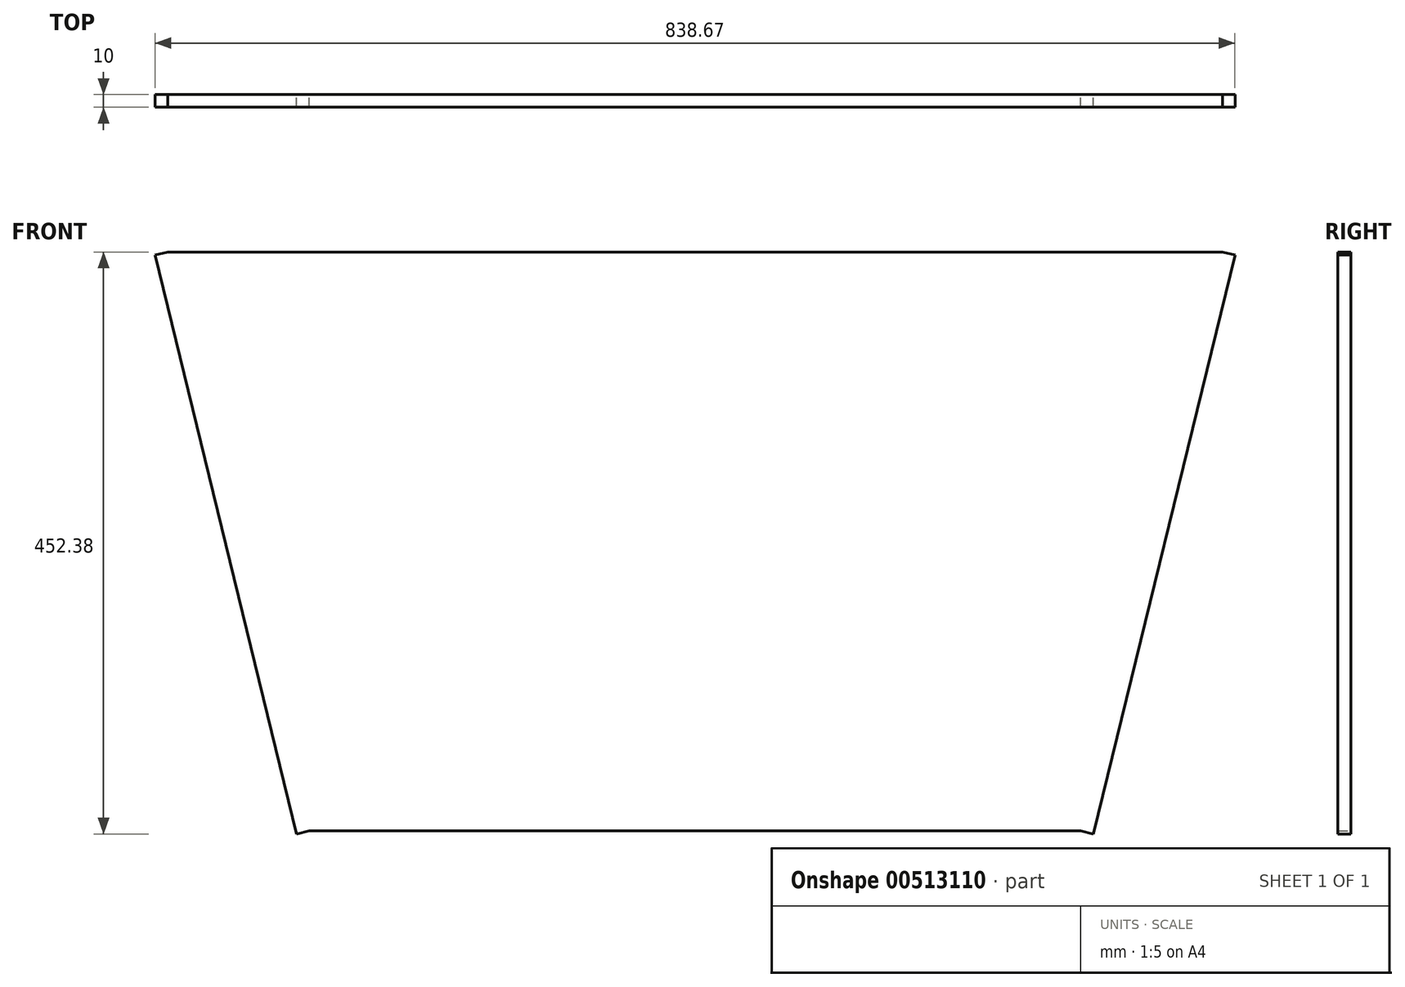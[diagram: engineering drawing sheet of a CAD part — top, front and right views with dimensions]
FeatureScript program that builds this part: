
annotation { "Feature Type Name" : "Feature", "Feature Type Description" : "" }
export const myFeature = defineFeature(function(context is Context, id is Id, definition is map)
    precondition{}
    {
        {
            var Q0;
            Q0=qCreatedBy(makeId("Front.planeOp"),FACE);
            var sketch = newSketch(context, id + "F0", { "sketchPlane" : qUnion([Q0])});
            skLineSegment(sketch, "E0.1", {"start": v(-436.34, 213.95) * mm, "end": v(-436.34, -176.05) * mm});
            skLineSegment(sketch, "E0.3", {"start": v(103.66, 213.95) * mm, "end": v(103.66, -176.05) * mm});
            skLineSegment(sketch, "E1", {"start": v(-465.58, -206.05) * mm, "end": v(133.66, -206.05) * mm});
            skLineSegment(sketch, "E2", {"start": v(-436.34, -176.05) * mm, "end": v(103.66, -176.05) * mm});
            skLineSegment(sketch, "E3", {"start": v(-436.34, 213.95) * mm, "end": v(103.66, 213.95) * mm});
            skLineSegment(sketch, "E4", {"start": v(-465.58, 243.95) * mm, "end": v(133.66, 243.95) * mm});
            skLineSegment(sketch, "E5", {"start": v(-465.58, 243.95) * mm, "end": v(-575.58, 243.95) * mm});
            skLineSegment(sketch, "E6", {"start": v(133.66, 243.95) * mm, "end": v(243.66, 243.95) * mm});
            skLineSegment(sketch, "E7", {"start": v(-575.58, 243.95) * mm, "end": v(-465.58, -206.05) * mm});
            skLineSegment(sketch, "E8", {"start": v(243.66, 243.95) * mm, "end": v(133.66, -206.05) * mm});
            skLineSegment(sketch, "E9.0", {"start": v(-537.36, 213.95) * mm, "end": v(-495.58, 43.02) * mm});
            skLineSegment(sketch, "E9.1", {"start": v(-495.58, 213.95) * mm, "end": v(-537.36, 213.95) * mm});
            skLineSegment(sketch, "E9.2", {"start": v(-495.58, 213.95) * mm, "end": v(-495.58, 43.02) * mm});
            skLineSegment(sketch, "E10.0", {"start": v(205.44, 213.95) * mm, "end": v(163.66, 43.02) * mm});
            skLineSegment(sketch, "E10.1", {"start": v(163.66, 213.95) * mm, "end": v(205.44, 213.95) * mm});
            skLineSegment(sketch, "E10.2", {"start": v(163.66, 213.95) * mm, "end": v(163.66, 43.02) * mm});
            skSolve(sketch);
        }
        {
            var Q0;
            Q0=makeQuery(id+"F0.imprint","IMPRINT",FACE,{"disambiguationData":[TD([[makeQuery(id+"F0.imprint","IMPRINT",EDGE,{"derivedFrom":sQuery(id+"F0.wireOp",EDGE,"E0.1")}),-1.0]])]});
            extrude(context, id + "F1", {"entities" : qUnion([Q0]), "depth" : 10 * mm, "offsetDistance" : 25 * mm});
        }
        {
            var Q0;
            Q0=makeQuery(id+"F1.opExtrude","CAP_FACE",FACE,{"disambiguationData":[OSD([sQuery(id+"F0.wireOp",EDGE,"E0.1"),sQuery(id+"F0.wireOp",EDGE,"E0.3"),sQuery(id+"F0.wireOp",EDGE,"E1"),sQuery(id+"F0.wireOp",EDGE,"E2"),sQuery(id+"F0.wireOp",EDGE,"E3"),sQuery(id+"F0.wireOp",EDGE,"E4"),sQuery(id+"F0.wireOp",EDGE,"E5"),sQuery(id+"F0.wireOp",EDGE,"E6"),sQuery(id+"F0.wireOp",EDGE,"E7"),sQuery(id+"F0.wireOp",EDGE,"E8"),sQuery(id+"F0.wireOp",EDGE,"E9.0"),sQuery(id+"F0.wireOp",EDGE,"E9.1"),sQuery(id+"F0.wireOp",EDGE,"E9.2"),sQuery(id+"F0.wireOp",EDGE,"E10.0"),sQuery(id+"F0.wireOp",EDGE,"E10.1"),sQuery(id+"F0.wireOp",EDGE,"E10.2")])],"isStart":false});
            var sketch = newSketch(context, id + "F2", { "sketchPlane" : qUnion([Q0])});
            skLineSegment(sketch, "E11.bottom", {"start": v(-436.34, 213.95) * mm, "end": v(-356.34, 213.95) * mm});
            skLineSegment(sketch, "E11.top", {"start": v(-436.34, 133.95) * mm, "end": v(-356.34, 133.95) * mm});
            skLineSegment(sketch, "E11.left", {"start": v(-436.34, 213.95) * mm, "end": v(-436.34, 133.95) * mm});
            skLineSegment(sketch, "E11.right", {"start": v(-356.34, 213.95) * mm, "end": v(-356.34, 133.95) * mm});
            skLineSegment(sketch, "E12.bottom", {"start": v(103.66, 213.95) * mm, "end": v(23.66, 213.95) * mm});
            skLineSegment(sketch, "E12.top", {"start": v(103.66, 133.95) * mm, "end": v(23.66, 133.95) * mm});
            skLineSegment(sketch, "E12.left", {"start": v(103.66, 213.95) * mm, "end": v(103.66, 133.95) * mm});
            skLineSegment(sketch, "E12.right", {"start": v(23.66, 213.95) * mm, "end": v(23.66, 133.95) * mm});
            skLineSegment(sketch, "E13.bottom", {"start": v(-436.34, -176.05) * mm, "end": v(-356.34, -176.05) * mm});
            skLineSegment(sketch, "E13.top", {"start": v(-436.34, -96.05) * mm, "end": v(-356.34, -96.05) * mm});
            skLineSegment(sketch, "E13.left", {"start": v(-436.34, -176.05) * mm, "end": v(-436.34, -96.05) * mm});
            skLineSegment(sketch, "E13.right", {"start": v(-356.34, -176.05) * mm, "end": v(-356.34, -96.05) * mm});
            skLineSegment(sketch, "E14.bottom", {"start": v(103.66, -176.05) * mm, "end": v(23.66, -176.05) * mm});
            skLineSegment(sketch, "E14.top", {"start": v(103.66, -96.05) * mm, "end": v(23.66, -96.05) * mm});
            skLineSegment(sketch, "E14.left", {"start": v(103.66, -176.05) * mm, "end": v(103.66, -96.05) * mm});
            skLineSegment(sketch, "E14.right", {"start": v(23.66, -176.05) * mm, "end": v(23.66, -96.05) * mm});
            skCircle(sketch, "E15", {"center": v(-396.34, -136.05) * mm, "radius": 15 * mm});
            skCircle(sketch, "E16", {"center": v(-396.34, 198.82) * mm, "radius": 15 * mm});
            skCircle(sketch, "E17", {"center": v(63.66, 198.82) * mm, "radius": 15 * mm});
            skCircle(sketch, "E18", {"center": v(63.66, -136.05) * mm, "radius": 15 * mm});
            skSolve(sketch);
        }
        {
            var Q0;
            Q0=makeQuery(id+"F2.imprint","IMPRINT",FACE,{"disambiguationData":[TD([[makeQuery(id+"F2.imprint","IMPRINT",EDGE,{"derivedFrom":sQuery(id+"F2.wireOp",EDGE,"E11.bottom")}),-1.0]])]});
            var Q1;
            Q1=makeQuery(id+"F2.imprint","IMPRINT",FACE,{"disambiguationData":[TD([[makeQuery(id+"F2.imprint","IMPRINT",EDGE,{"derivedFrom":sQuery(id+"F2.wireOp",EDGE,"E12.bottom")}),-1.0]])]});
            var Q2;
            Q2=makeQuery(id+"F2.imprint","IMPRINT",FACE,{"disambiguationData":[TD([[makeQuery(id+"F2.imprint","IMPRINT",EDGE,{"derivedFrom":sQuery(id+"F2.wireOp",EDGE,"E14.bottom")}),1.0]])]});
            var Q3;
            Q3=makeQuery(id+"F2.imprint","IMPRINT",FACE,{"disambiguationData":[TD([[makeQuery(id+"F2.imprint","IMPRINT",EDGE,{"derivedFrom":sQuery(id+"F2.wireOp",EDGE,"E13.bottom")}),1.0]])]});
            extrude(context, id + "F3", {"entities" : qUnion([Q0, Q1, Q2, Q3]), "operationType" : NewBodyOperationType.ADD, "oppositeDirection" : true, "depth" : 10 * mm, "offsetDistance" : 25 * mm});
        }
        {
            var Q0;
            Q0=makeQuery(id+"F3.boolean.opBoolean","MERGE",FACE,{"derivedFrom":[makeQuery(id+"F1.opExtrude","CAP_FACE",FACE,{"disambiguationData":[OSD([sQuery(id+"F0.wireOp",EDGE,"E0.1"),sQuery(id+"F0.wireOp",EDGE,"E0.3"),sQuery(id+"F0.wireOp",EDGE,"E1"),sQuery(id+"F0.wireOp",EDGE,"E2"),sQuery(id+"F0.wireOp",EDGE,"E3"),sQuery(id+"F0.wireOp",EDGE,"E4"),sQuery(id+"F0.wireOp",EDGE,"E5"),sQuery(id+"F0.wireOp",EDGE,"E6"),sQuery(id+"F0.wireOp",EDGE,"E7"),sQuery(id+"F0.wireOp",EDGE,"E8"),sQuery(id+"F0.wireOp",EDGE,"E9.0"),sQuery(id+"F0.wireOp",EDGE,"E9.1"),sQuery(id+"F0.wireOp",EDGE,"E9.2"),sQuery(id+"F0.wireOp",EDGE,"E10.0"),sQuery(id+"F0.wireOp",EDGE,"E10.1"),sQuery(id+"F0.wireOp",EDGE,"E10.2")])],"isStart":false}),makeQuery(id+"F3.opExtrude","CAP_FACE",FACE,{"disambiguationData":[OSD([sQuery(id+"F2.wireOp",EDGE,"E11.bottom"),sQuery(id+"F2.wireOp",EDGE,"E11.top"),sQuery(id+"F2.wireOp",EDGE,"E11.left"),sQuery(id+"F2.wireOp",EDGE,"E11.right"),sQuery(id+"F2.wireOp",EDGE,"E16")])],"isStart":true}),makeQuery(id+"F3.opExtrude","CAP_FACE",FACE,{"disambiguationData":[OSD([sQuery(id+"F2.wireOp",EDGE,"E12.bottom"),sQuery(id+"F2.wireOp",EDGE,"E12.top"),sQuery(id+"F2.wireOp",EDGE,"E12.left"),sQuery(id+"F2.wireOp",EDGE,"E12.right"),sQuery(id+"F2.wireOp",EDGE,"E17")])],"isStart":true}),makeQuery(id+"F3.opExtrude","CAP_FACE",FACE,{"disambiguationData":[OSD([sQuery(id+"F2.wireOp",EDGE,"E13.bottom"),sQuery(id+"F2.wireOp",EDGE,"E13.top"),sQuery(id+"F2.wireOp",EDGE,"E13.left"),sQuery(id+"F2.wireOp",EDGE,"E13.right"),sQuery(id+"F2.wireOp",EDGE,"E15")])],"isStart":true}),makeQuery(id+"F3.opExtrude","CAP_FACE",FACE,{"disambiguationData":[OSD([sQuery(id+"F2.wireOp",EDGE,"E14.bottom"),sQuery(id+"F2.wireOp",EDGE,"E14.top"),sQuery(id+"F2.wireOp",EDGE,"E14.left"),sQuery(id+"F2.wireOp",EDGE,"E14.right"),sQuery(id+"F2.wireOp",EDGE,"E18")])],"isStart":true})]});
            var sketch = newSketch(context, id + "F4", { "sketchPlane" : qUnion([Q0])});
            skLineSegment(sketch, "E19", {"start": v(-575.58, 243.95) * mm, "end": v(-465.58, -206.05) * mm});
            skLineSegment(sketch, "E20", {"start": v(-465.58, -206.05) * mm, "end": v(133.66, -206.05) * mm});
            skLineSegment(sketch, "E21", {"start": v(133.66, -206.05) * mm, "end": v(243.66, 243.95) * mm});
            skLineSegment(sketch, "E22", {"start": v(243.66, 243.95) * mm, "end": v(-575.58, 243.95) * mm});
            skSolve(sketch);
        }
        {
            var Q0;
            Q0=makeQuery(id+"F4.imprint","IMPRINT",FACE,{"disambiguationData":[TD([[makeQuery(id+"F4.imprint","IMPRINT",EDGE,{"derivedFrom":makeQuery(id+"F1.opExtrude","CAP_EDGE",EDGE,{"disambiguationData":[OSD([sQuery(id+"F0.wireOp",EDGE,"E9.0")])],"isStart":false})}),1.0]])]});
            var Q1;
            Q1=makeQuery(id+"F4.imprint","IMPRINT",FACE,{"disambiguationData":[TD([[makeQuery(id+"F4.imprint","IMPRINT",EDGE,{"derivedFrom":makeQuery(id+"F3.opExtrude","CAP_EDGE",EDGE,{"disambiguationData":[OSD([sQuery(id+"F2.wireOp",EDGE,"E11.top")])],"isStart":true})}),-1.0]])]});
            var Q2;
            Q2=makeQuery(id+"F4.imprint","IMPRINT",FACE,{"disambiguationData":[TD([[makeQuery(id+"F4.imprint","IMPRINT",EDGE,{"derivedFrom":makeQuery(id+"F3.opExtrude","CAP_EDGE",EDGE,{"disambiguationData":[OSD([sQuery(id+"F2.wireOp",EDGE,"E17")])],"isStart":true})}),1.0]])]});
            var Q3;
            Q3=makeQuery(id+"F4.imprint","IMPRINT",FACE,{"disambiguationData":[TD([[makeQuery(id+"F4.imprint","IMPRINT",EDGE,{"derivedFrom":sQuery(id+"F4.wireOp",EDGE,"E19")}),1.0]])]});
            var Q4;
            Q4=makeQuery(id+"F4.imprint","IMPRINT",FACE,{"disambiguationData":[TD([[makeQuery(id+"F4.imprint","IMPRINT",EDGE,{"derivedFrom":makeQuery(id+"F3.opExtrude","CAP_EDGE",EDGE,{"disambiguationData":[OSD([sQuery(id+"F2.wireOp",EDGE,"E16")])],"isStart":true})}),1.0]])]});
            var Q5;
            Q5=makeQuery(id+"F4.imprint","IMPRINT",FACE,{"disambiguationData":[TD([[makeQuery(id+"F4.imprint","IMPRINT",EDGE,{"derivedFrom":makeQuery(id+"F3.opExtrude","CAP_EDGE",EDGE,{"disambiguationData":[OSD([sQuery(id+"F2.wireOp",EDGE,"E15")])],"isStart":true})}),1.0]])]});
            var Q6;
            Q6=makeQuery(id+"F4.imprint","IMPRINT",FACE,{"disambiguationData":[TD([[makeQuery(id+"F4.imprint","IMPRINT",EDGE,{"derivedFrom":makeQuery(id+"F3.opExtrude","CAP_EDGE",EDGE,{"disambiguationData":[OSD([sQuery(id+"F2.wireOp",EDGE,"E18")])],"isStart":true})}),1.0]])]});
            var Q7;
            Q7=makeQuery(id+"F4.imprint","IMPRINT",FACE,{"disambiguationData":[TD([[makeQuery(id+"F4.imprint","IMPRINT",EDGE,{"derivedFrom":makeQuery(id+"F1.opExtrude","CAP_EDGE",EDGE,{"disambiguationData":[OSD([sQuery(id+"F0.wireOp",EDGE,"E10.0")])],"isStart":false})}),-1.0]])]});
            extrude(context, id + "F5", {"entities" : qUnion([Q0, Q1, Q2, Q3, Q4, Q5, Q6, Q7]), "operationType" : NewBodyOperationType.ADD, "oppositeDirection" : true, "depth" : 10 * mm, "offsetDistance" : 25 * mm});
        }
        {
            var Q0;
            Q0=makeQuery(id+"F1.opExtrude","SWEPT_FACE",FACE,{"disambiguationData":[OSD([sQuery(id+"F0.wireOp",EDGE,"E7")])]});
            extrude(context, id + "F6", {"entities" : qUnion([Q0]), "operationType" : NewBodyOperationType.ADD, "depth" : 10 * mm, "offsetDistance" : 25 * mm});
        }
        {
            var Q0;
            Q0=makeQuery(id+"F1.opExtrude","SWEPT_FACE",FACE,{"disambiguationData":[OSD([sQuery(id+"F0.wireOp",EDGE,"E8")])]});
            extrude(context, id + "F7", {"entities" : qUnion([Q0]), "operationType" : NewBodyOperationType.ADD, "depth" : 10 * mm, "offsetDistance" : 25 * mm});
        }
    });
